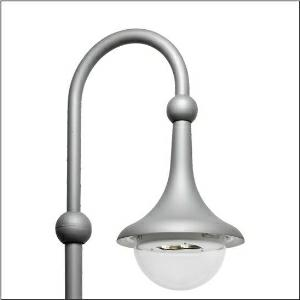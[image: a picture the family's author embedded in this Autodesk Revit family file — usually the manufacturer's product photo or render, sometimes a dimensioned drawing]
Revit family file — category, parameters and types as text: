
# Revit family: grosse_glocke___st1_2a_5xa1563e1b108_a6a2
name_source: partatom
category: Lighting Fixtures
units: mm (PartAtom-declared; Revit-internal decimal feet)

## family parameters
Cut with Voids When Loaded = No
Host = Face
Light Source = No
Part Type = Normal
Room Calculation Point = No
Round Connector Dimension = Use Diameter
Shared = No

## types (1)
- --- (1 x LED, 3150 lm, 23.4 W, 3000K)
    Apparent Load = 23 VA
    CIE Flux Codes = 29 66 95 99 100
    Color Rendering = 70
    Color Temperature = 3000K
    Default Elevation = 1800 mm
    Description = Large Bell, mast luminaire, primary light control with 3 zone facetted reflector, of plastic, silver coated, primary optical cover: enclosure, of PMMA, transparent, light distribution: ST1.2a, light emission: direct distribution, primary light characteristic: asymmetric, installation type: suspended mounting, LED High Power LED, rated luminous flux: 3.150 lm, light colour: 730, colour temperature: 3000K, control gear: ECG Plus, control: flexible luminous flux parameterisation, time-dependent luminous flux control, constant luminous flux control, digital communication interface, power reduction, electronic power reduction, mains connection: 220..240V, AC, 50/60Hz, start of lifetime: 23 W, end of lifetime: 24 W, reduction: 12 W, luminaire housing, bell-shaped, of glass-fibre reinforced polyester, coated, Siteco® metallic grey (DB 702S), diameter: 530 mm, height: 695mm, protection rating (complete): IP54, insulation class (complete): insulation class II (safety insulation), certification: CE, ENEC, VDE, impact resistance: IK08, standard-compliant lighting for roads and squares, packaging unit: 1 piece

Light Distribution: ST1.2a
    Height = 695 mm
    Lamp = 1 x LED
    Lamp Light Flux = 3150 lm
    Lamp Power = 23.4 W
    Lamp count = 1
    Length = 530 mm
    Luminous efficacy = 135 lm/W
    Manufacturer = Siteco
    ModVariant = No
    Model = 5XA1563E1B108
    Number of Poles = 1
    OnlyDefault = Yes
    Power Factor = 1
    Product Name = Große Glocke | ST1.2a
    Product group = mast luminaire | pylon annexe
    ProductGroupID = 6200
    Protection Class = Protection class II
    Protection Degree = IP 54
    RLX_Detail_Level = 1
    RlxData = <blob elided: 52661 chars, md5=47d8071c>
    Socket = socket
    Standby Power = 0 W
    System Light Flux = 3150 lm
    System Power = 23 W
    Type Comments = factory setting: luminous flux: 100 % | dim-lin: 254 | 460 mA
    Type Image = l_1005953.jpg
    URL = http://relux.com
    VarID = @adj_070209
    Voltage = 0 V
    Weight = 0.00 kg
    Width = 0 mm  [stored 0 ft]

note: [stored X ft] marks values corroborated as IEEE doubles in the binary element streams (Revit-internal decimal feet)

## geometry (parser evidence)
native form markers: Blend x4, Sweep x11
no freeform markers — native parametric forms only
